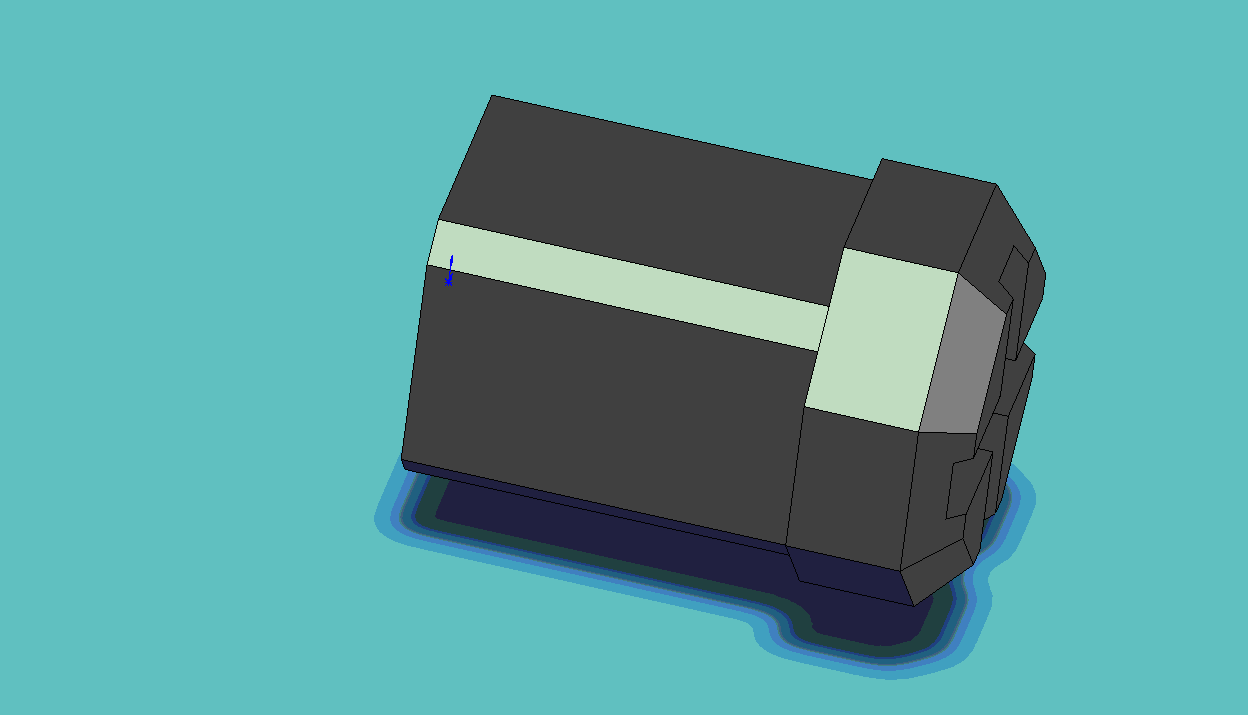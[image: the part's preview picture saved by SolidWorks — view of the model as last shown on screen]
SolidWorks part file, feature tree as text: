
SOLIDWORKS PART (.sldprt)
format: sldprt  version: not decoded by parser v0  size: 275,456 bytes
history: native  units: mm
features: plane x3, sketch x3, chamfer x3, extrude x2, material x1, cut_extrude x1 (+10 scaffold rows collapsed)
feature tree (23):
  scaffold x10  (default folders/planes/origin — collapsed)
  material  "Matériau <non spécifié>"
  plane  "Plan de face"
  plane  "Plan de dessus"
  plane  "Plan de droite"
  sketch  "Esquisse1"  dims[D1=9.0mm D2=9.0mm]
  extrude  "Extrusion1"  Depth=12mm
  sketch  "Esquisse2"  dims[D2=12.0mm D1=1.5mm]
  extrude  "Extrusion2"  Depth=5mm
  chamfer  "Chanfrein3"  Distance=1mm Angle=45deg
  chamfer  "Chanfrein1"  Distance=3.5mm Angle=45deg
  chamfer  "Chanfrein2"  Distance=1.5mm Angle=45deg
  sketch  "Esquisse3"  dims[D1=10.0mm D2=2.0mm D3=1.0mm D4=1.0mm D5=5.0mm D6=5.0mm]
  cut_extrude  "Enlèv. mat.-Extru.1"  Depth=1.5mm
decode coverage: 9 of 9 modeling features carry decoded parameters
note: suppression state not decoded; provenance and decode notes live in map.json
